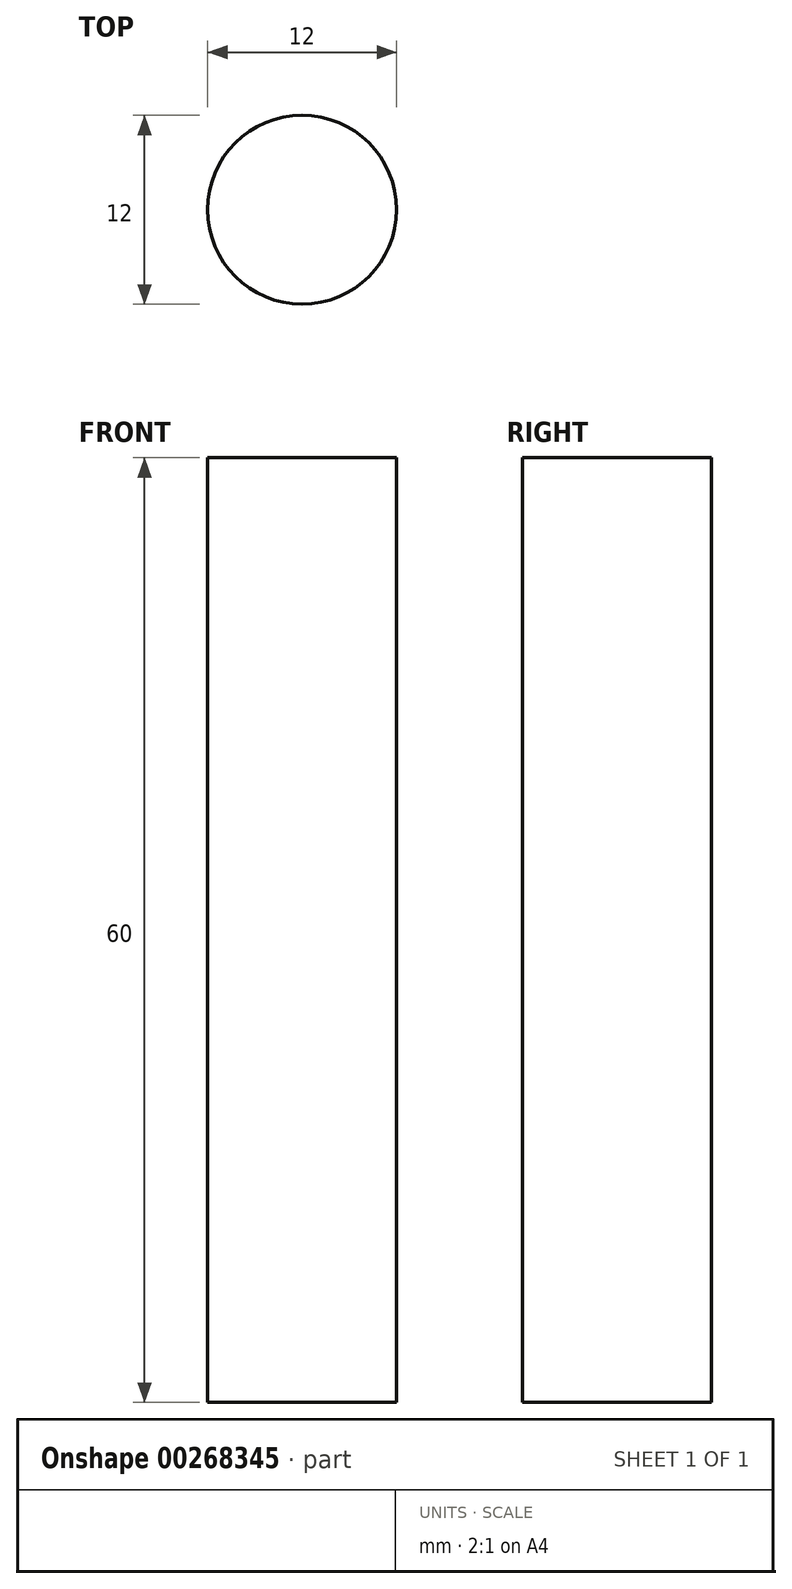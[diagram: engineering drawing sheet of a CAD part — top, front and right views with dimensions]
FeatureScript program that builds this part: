
annotation { "Feature Type Name" : "Feature", "Feature Type Description" : "" }
export const myFeature = defineFeature(function(context is Context, id is Id, definition is map)
    precondition{}
    {
        {
            var Q0;
            Q0=qCreatedBy(makeId("Top.planeOp"),FACE);
            var sketch = newSketch(context, id + "F0", { "sketchPlane" : qUnion([Q0])});
            skCircle(sketch, "E0", {"center": v(0, 0) * mm, "radius": 6 * mm});
            skSolve(sketch);
        }
        {
            var Q0;
            Q0=qSketchRegion(id+"F0",true);
            extrude(context, id + "F1", {"entities" : qUnion([Q0]), "depth" : 60 * mm});
        }
    });
